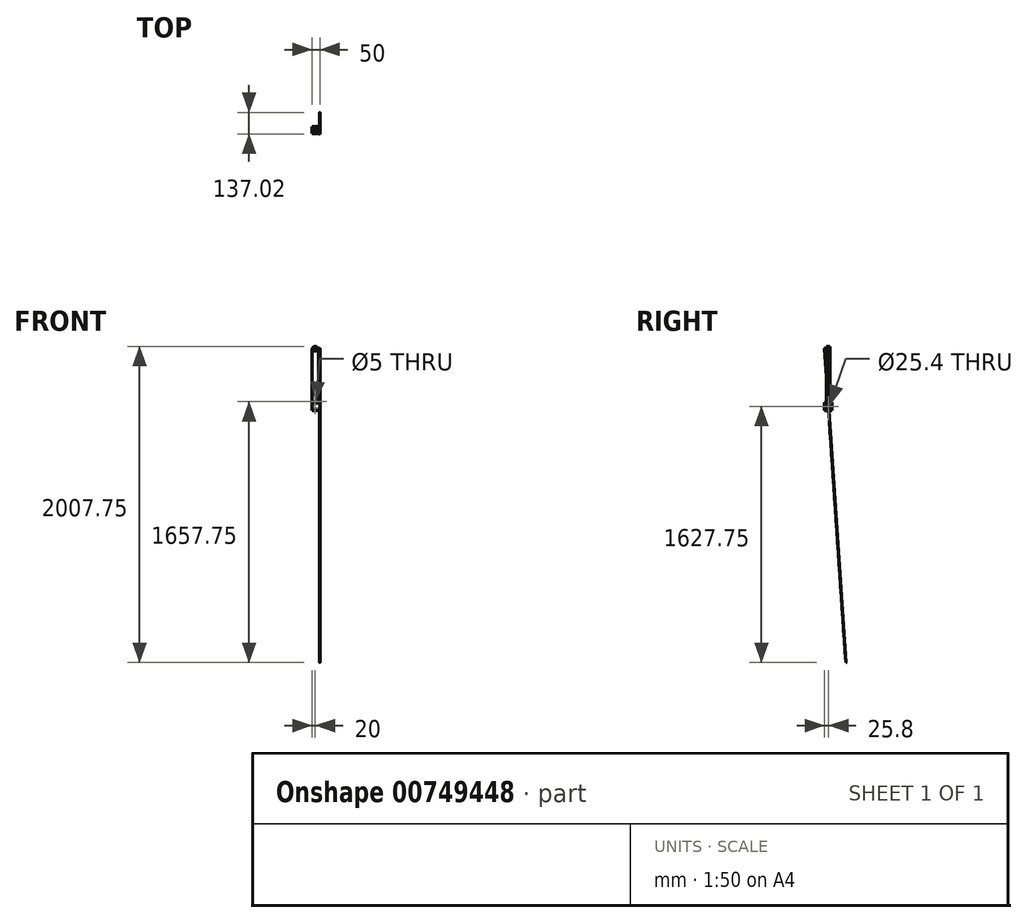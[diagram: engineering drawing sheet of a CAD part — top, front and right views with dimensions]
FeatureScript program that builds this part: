
annotation { "Feature Type Name" : "Feature", "Feature Type Description" : "" }
export const myFeature = defineFeature(function(context is Context, id is Id, definition is map)
    precondition{}
    {
        {
            var Q0;
            Q0=qCreatedBy(makeId("Front.planeOp"),FACE);
            var sketch = newSketch(context, id + "F0", { "sketchPlane" : qUnion([Q0])});
            skLineSegment(sketch, "E0.bottom", {"start": v(0, 0) * mm, "end": v(40, 0) * mm});
            skLineSegment(sketch, "E0.top", {"start": v(20, 405) * mm, "end": v(20, 405) * mm});
            skLineSegment(sketch, "E0.left", {"start": v(0, 0) * mm, "end": v(0, 385) * mm});
            skLineSegment(sketch, "E0.right", {"start": v(40, 0) * mm, "end": v(40, 385) * mm});
            skPoint(sketch, "E1.visualSharp", {"position": v(0, 405) * mm});
            skArc(sketch, "E1.filletArc", {"start": v(20, 405) * mm, "mid": v(5.86, 399.14) * mm, "end": v(0, 385) * mm});
            skPoint(sketch, "E2.visualSharp", {"position": v(40, 405) * mm});
            skArc(sketch, "E2.filletArc", {"start": v(40, 385) * mm, "mid": v(34.14, 399.14) * mm, "end": v(20, 405) * mm});
            skSolve(sketch);
        }
        {
            var Q0;
            Q0=makeQuery(id+"F0.imprint","IMPRINT",FACE,{"disambiguationData":[TD([[makeQuery(id+"F0.imprint","IMPRINT",EDGE,{"derivedFrom":sQuery(id+"F0.wireOp",EDGE,"E0.bottom")}),1.0]])]});
            extrude(context, id + "F1", {"entities" : qUnion([Q0]), "depth" : 22 * mm, "offsetDistance" : 25 * mm});
        }
        {
            var Q0;
            Q0=makeQuery(id+"F1.opExtrude","CAP_FACE",FACE,{"disambiguationData":[OSD([sQuery(id+"F0.wireOp",EDGE,"E0.bottom"),sQuery(id+"F0.wireOp",EDGE,"E0.left"),sQuery(id+"F0.wireOp",EDGE,"E0.right"),sQuery(id+"F0.wireOp",EDGE,"E1.filletArc"),sQuery(id+"F0.wireOp",EDGE,"E2.filletArc")])],"isStart":false});
            var sketch = newSketch(context, id + "F2", { "sketchPlane" : qUnion([Q0])});
            skCircle(sketch, "E3", {"center": v(20, 385) * mm, "radius": 8.15 * mm});
            skSolve(sketch);
        }
        {
            var Q0;
            Q0=makeQuery(id+"F2.imprint","IMPRINT",FACE,{"disambiguationData":[TD([[makeQuery(id+"F2.imprint","IMPRINT",EDGE,{"derivedFrom":sQuery(id+"F2.wireOp",EDGE,"E3")}),1.0]])]});
            extrude(context, id + "F3", {"entities" : qUnion([Q0]), "operationType" : NewBodyOperationType.REMOVE, "endBound" : BoundingType.THROUGH_ALL, "oppositeDirection" : true, "depth" : 25 * mm, "offsetDistance" : 25 * mm, "hasDraft" : true, "draftAngle" : 5.72 * degree, "draftPullDirection" : true});
        }
        {
            var Q0;
            Q0=makeQuery(id+"F1.opExtrude","CAP_FACE",FACE,{"disambiguationData":[OSD([sQuery(id+"F0.wireOp",EDGE,"E0.bottom"),sQuery(id+"F0.wireOp",EDGE,"E0.left"),sQuery(id+"F0.wireOp",EDGE,"E0.right"),sQuery(id+"F0.wireOp",EDGE,"E1.filletArc"),sQuery(id+"F0.wireOp",EDGE,"E2.filletArc")])],"isStart":false});
            var sketch = newSketch(context, id + "F4", { "sketchPlane" : qUnion([Q0])});
            skLineSegment(sketch, "E4.bottom", {"start": v(0, 0) * mm, "end": v(40, 0) * mm});
            skLineSegment(sketch, "E4.top", {"start": v(0, 50) * mm, "end": v(40, 50) * mm});
            skLineSegment(sketch, "E4.left", {"start": v(0, 0) * mm, "end": v(0, 50) * mm});
            skLineSegment(sketch, "E4.right", {"start": v(40, 0) * mm, "end": v(40, 50) * mm});
            skSolve(sketch);
        }
        {
            var Q0;
            Q0 = qSketchRegion(id + "F4", true);
            extrude(context, id + "F5", {"entities" : qUnion([Q0]), "operationType" : NewBodyOperationType.ADD, "depth" : 12.5 * mm, "offsetDistance" : 25 * mm, "hasSecondDirection" : true, "secondDirectionOppositeDirection" : true, "secondDirectionDepth" : 34.5 * mm});
        }
        {
            var Q0;
            Q0=makeQuery(id+"F5.boolean.opBoolean","MERGE",FACE,{"derivedFrom":[makeQuery(id+"F1.opExtrude","SWEPT_FACE",FACE,{"disambiguationData":[OSD([sQuery(id+"F0.wireOp",EDGE,"E0.left")])]}),makeQuery(id+"F5.opExtrude","SWEPT_FACE",FACE,{"disambiguationData":[OSD([sQuery(id+"F4.wireOp",EDGE,"E4.left")])]})]});
            var sketch = newSketch(context, id + "F6", { "sketchPlane" : qUnion([Q0])});
            skCircle(sketch, "E5", {"center": v(10, 25) * mm, "radius": 12.7 * mm});
            skSolve(sketch);
        }
        {
            var Q0;
            Q0 = qSketchRegion(id + "F6", true);
            extrude(context, id + "F7", {"entities" : qUnion([Q0]), "operationType" : NewBodyOperationType.REMOVE, "endBound" : BoundingType.THROUGH_ALL, "oppositeDirection" : true, "depth" : 25 * mm, "offsetDistance" : 25 * mm});
        }
        {
            var Q0;
            Q0=makeQuery(id+"F5.boolean.opBoolean","MERGE",FACE,{"derivedFrom":[makeQuery(id+"F1.opExtrude","SWEPT_FACE",FACE,{"disambiguationData":[OSD([sQuery(id+"F0.wireOp",EDGE,"E0.right")])]}),makeQuery(id+"F5.opExtrude","SWEPT_FACE",FACE,{"disambiguationData":[OSD([sQuery(id+"F4.wireOp",EDGE,"E4.right")])]})]});
            var sketch = newSketch(context, id + "F8", { "sketchPlane" : qUnion([Q0])});
            skLineSegment(sketch, "E6", {"start": v(-22, 50) * mm, "end": v(0, 50) * mm});
            skSolve(sketch);
        }
        {
            var Q0;
            Q0 = qSketchRegion(id + "F8", true);
            var Q1;
            Q1=makeQuery(id+"F8.imprint","IMPRINT",FACE,{"disambiguationData":[TD([[makeQuery(id+"F8.imprint","IMPRINT",EDGE,{"derivedFrom":sQuery(id+"F8.wireOp",EDGE,"E6")}),-1.0]])]});
            extrude(context, id + "F9", {"entities" : qUnion([Q0, Q1]), "operationType" : NewBodyOperationType.ADD, "depth" : 10 * mm, "offsetDistance" : 25 * mm});
        }
        {
            var Q0;
            Q0=makeQuery(id+"F1.opExtrude","CAP_FACE",FACE,{"disambiguationData":[OSD([sQuery(id+"F0.wireOp",EDGE,"E0.bottom"),sQuery(id+"F0.wireOp",EDGE,"E0.left"),sQuery(id+"F0.wireOp",EDGE,"E0.right"),sQuery(id+"F0.wireOp",EDGE,"E1.filletArc"),sQuery(id+"F0.wireOp",EDGE,"E2.filletArc")])],"isStart":false});
            var sketch = newSketch(context, id + "F10", { "sketchPlane" : qUnion([Q0])});
            skCircle(sketch, "E7", {"center": v(20, 55) * mm, "radius": 2.5 * mm});
            skSolve(sketch);
        }
        {
            var Q0;
            Q0=makeQuery(id+"F10.imprint","IMPRINT",FACE,{"disambiguationData":[TD([[makeQuery(id+"F10.imprint","IMPRINT",EDGE,{"derivedFrom":sQuery(id+"F10.wireOp",EDGE,"E7")}),1.0]])]});
            extrude(context, id + "F11", {"entities" : qUnion([Q0]), "operationType" : NewBodyOperationType.REMOVE, "oppositeDirection" : true, "depth" : 25 * mm, "offsetDistance" : 25 * mm});
        }
        {
            var Q0;
            Q0=makeQuery(id+"F9.opExtrude","CAP_FACE",FACE,{"disambiguationData":[OSD([sQuery(id+"F0.wireOp",EDGE,"E0.bottom"),sQuery(id+"F0.wireOp",EDGE,"E0.right"),sQuery(id+"F4.wireOp",EDGE,"E4.bottom"),sQuery(id+"F4.wireOp",EDGE,"E4.top"),sQuery(id+"F4.wireOp",EDGE,"E4.right"),sQuery(id+"F6.wireOp",EDGE,"E5"),sQuery(id+"F8.wireOp",EDGE,"E6")])],"isStart":false});
            var sketch = newSketch(context, id + "F12", { "sketchPlane" : qUnion([Q0])});
            skLineSegment(sketch, "E8", {"start": v(-10, 25) * mm, "end": v(-35.07, 392.67) * mm});
            skSolve(sketch);
        }
        {
            var Q0;
            Q0=sQuery(id+"F12.wireOp",VERTEX,"E8.end");
            var Q1;
            Q1=sQuery(id+"F12.wireOp",EDGE,"E8");
            cPlane(context, id + "F13", {"entities" : qUnion([Q0, Q1]), "cplaneType" : CPlaneType.LINE_POINT, "offset" : 25 * mm, "width" : 150 * mm, "height" : 150 * mm});
        }
        {
            var Q0;
            Q0=qCreatedBy(id+"F13.planeOp",FACE);
            var sketch = newSketch(context, id + "F14", { "sketchPlane" : qUnion([Q0])});
            skCircle(sketch, "E9", {"center": v(48.95, -8.52) * mm, "radius": 0.5 * mm});
            skSolve(sketch);
        }
        {
            var Q0;
            Q0 = qSketchRegion(id + "F14", true);
            extrude(context, id + "F15", {"entities" : qUnion([Q0]), "operationType" : NewBodyOperationType.ADD, "oppositeDirection" : true, "depth" : 2000 * mm, "offsetDistance" : 25 * mm});
        }
    });
